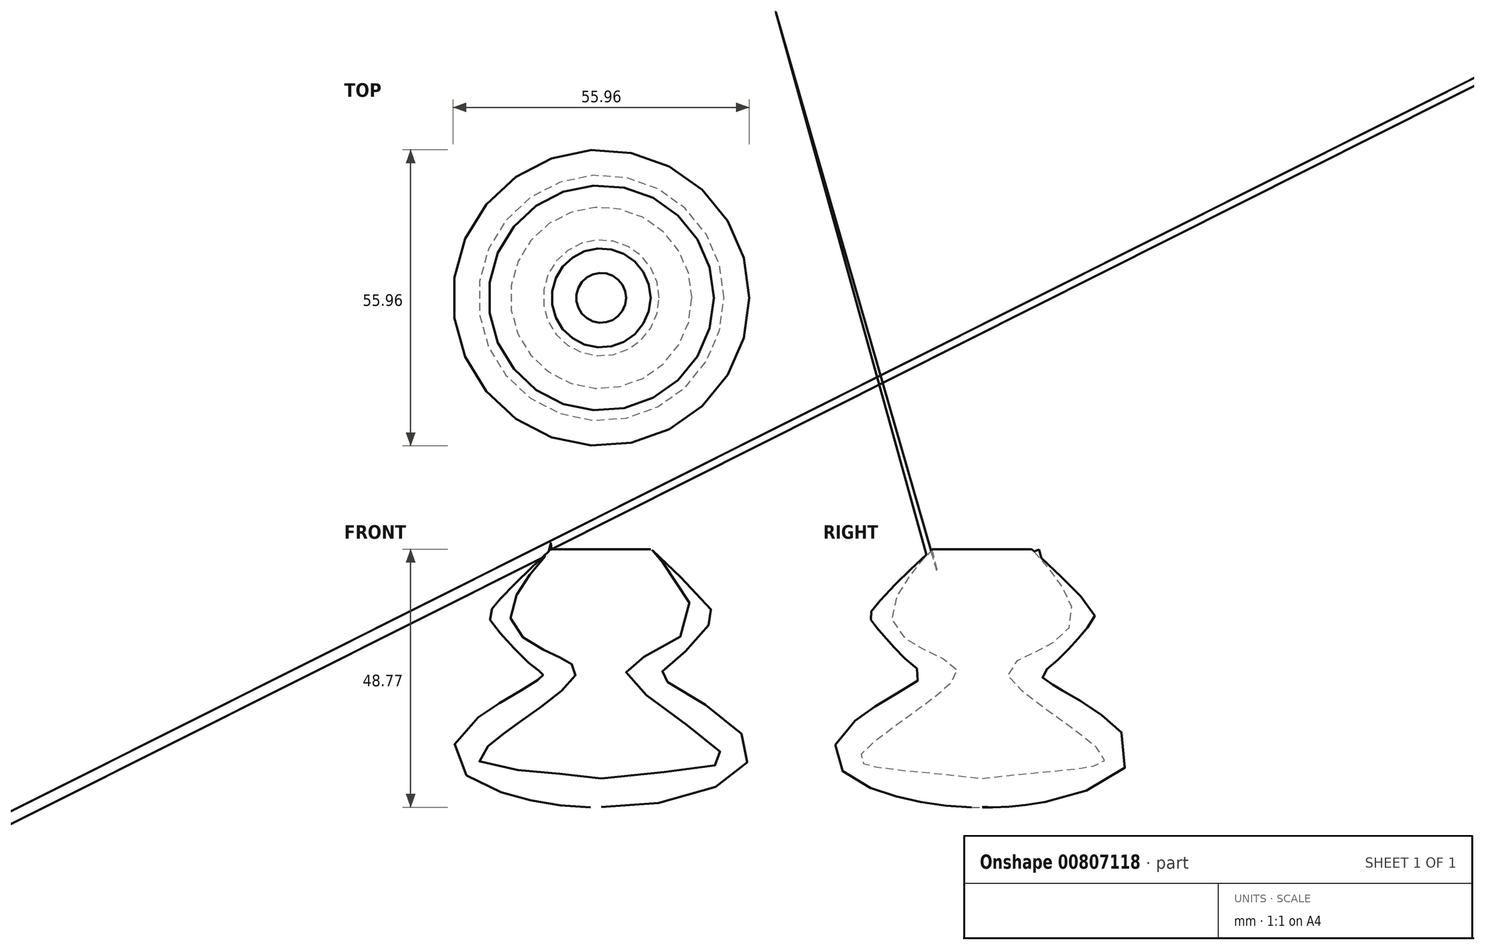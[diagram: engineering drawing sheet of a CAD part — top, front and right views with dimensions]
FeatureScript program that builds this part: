
annotation { "Feature Type Name" : "Feature", "Feature Type Description" : "" }
export const myFeature = defineFeature(function(context is Context, id is Id, definition is map)
    precondition{}
    {
        {
            var Q0;
            Q0=qCreatedBy(makeId("Front.planeOp"),FACE);
            var sketch = newSketch(context, id + "F0", { "sketchPlane" : qUnion([Q0])});
            skFitSpline(sketch, "E0", {"points": [v(9.35, 48.06) * mm, v(20.65, 36.76) * mm, v(20.65, 34.17) * mm, v(12.32, 25.47) * mm, v(11.02, 24.17) * mm, v(25.84, 13.98) * mm, v(25.65, 5.46) * mm, v(-3.8, 0) * mm, v(-5.65, 3.06) * mm, v(22.32, 7.5) * mm, v(22.5, 9.72) * mm, v(5.65, 23.06) * mm, v(5.65, 26.4) * mm, v(17.13, 35.28) * mm, v(9.35, 48.06) * mm]});
            skLineSegment(sketch, "E1", {"start": v(0, 64.22) * mm, "end": v(0, -6.5) * mm});
            skSolve(sketch);
        }
        {
            var Q0;
            {var subQ0=sQuery(id+"F0.wireOp",EDGE,"E1");var subQ1=sQuery(id+"F0.wireOp",EDGE,"E0");var subQ2=makeQuery(id+"F0.imprint","INTERSECT",VERTEX,{"disambiguationData":[OD(0.0)],"derivedFrom":[subQ1,subQ0]});Q0=makeQuery(id+"F0.imprint","IMPRINT",FACE,{"disambiguationData":[TD([[makeQuery(id+"F0.imprint","IMPRINT",EDGE,{"disambiguationData":[TD([[subQ2,-1.0]])],"derivedFrom":subQ1}),-1.0]])]});}
            var Q1;
            Q1=sQuery(id+"F0.wireOp",EDGE,"E1");
            revolve(context, id + "F1", {"surfaceOperationType" : NewSurfaceOperationType.NEW, "entities" : qUnion([Q0]), "axis" : qUnion([Q1]), "revolveType" : RevolveType.FULL, "oppositeDirection" : true});
        }
    });
